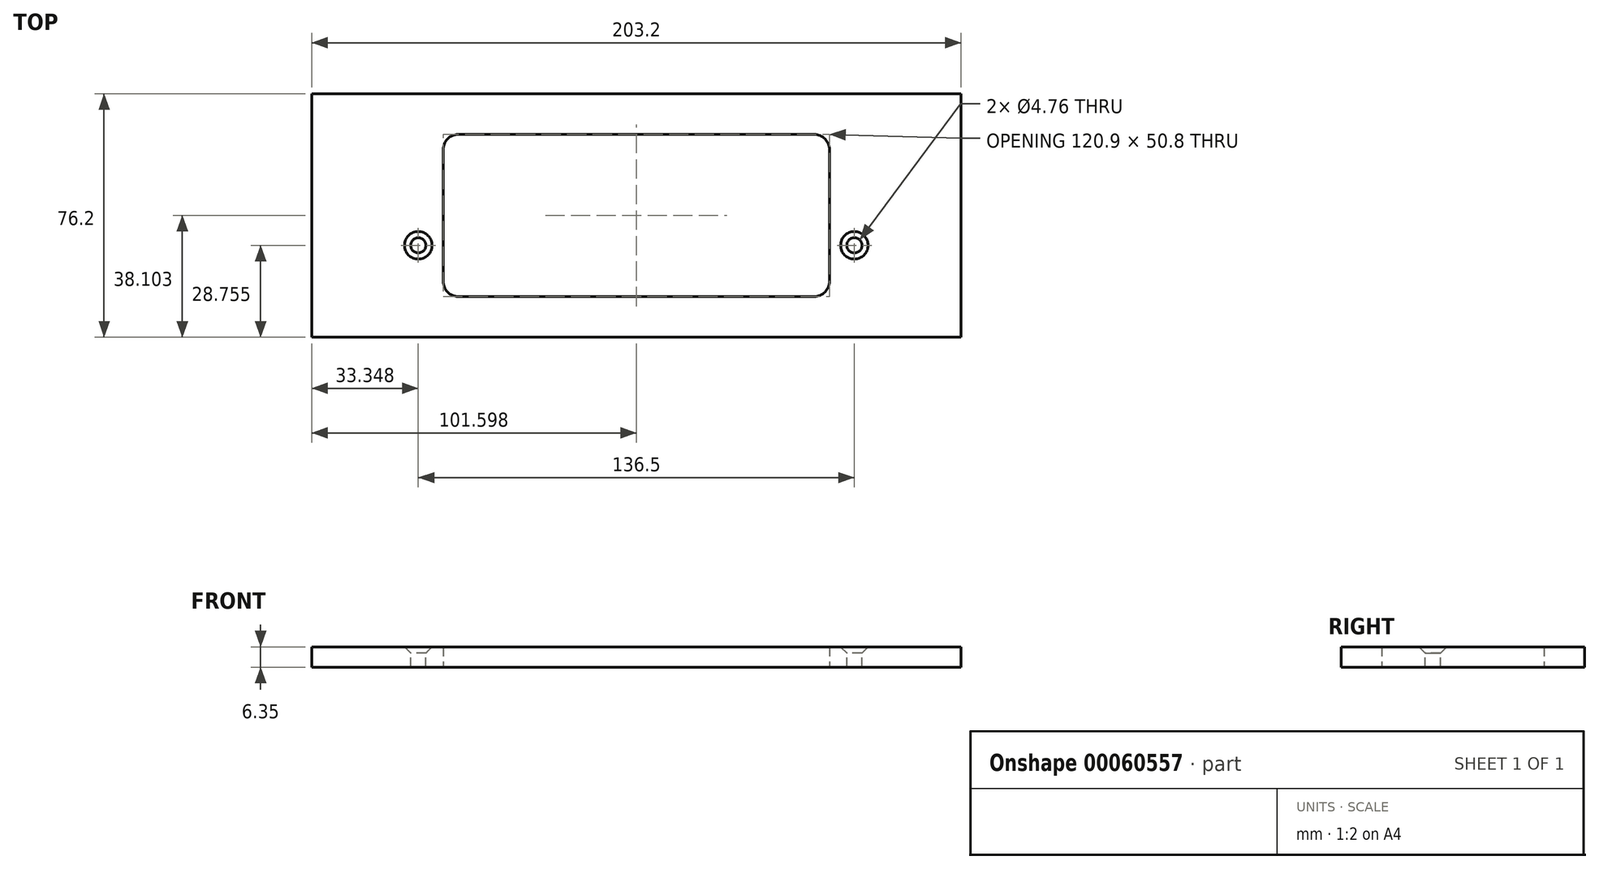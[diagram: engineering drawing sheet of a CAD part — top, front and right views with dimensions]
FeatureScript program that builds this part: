
annotation { "Feature Type Name" : "Feature", "Feature Type Description" : "" }
export const myFeature = defineFeature(function(context is Context, id is Id, definition is map)
    precondition{}
    {
        {
            var Q0;
            Q0=qCreatedBy(makeId("Top.planeOp"),FACE);
            var sketch = newSketch(context, id + "F0", { "sketchPlane" : qUnion([Q0])});
            skLineSegment(sketch, "E0.top", {"start": v(-103.7, -42.69) * mm, "end": v(99.5, -42.69) * mm});
            skLineSegment(sketch, "E0.left", {"start": v(-103.7, 33.51) * mm, "end": v(-103.7, -42.69) * mm});
            skLineSegment(sketch, "E0.right", {"start": v(99.5, 33.51) * mm, "end": v(99.5, -42.69) * mm});
            skPoint(sketch, "E1.rect.middle", {"position": v(0, 0) * mm});
            skLineSegment(sketch, "E2", {"start": v(-103.7, 33.51) * mm, "end": v(99.5, 33.51) * mm});
            skLineSegment(sketch, "E3.bottom", {"start": v(-57.78, 20.81) * mm, "end": v(53.6, 20.81) * mm});
            skLineSegment(sketch, "E3.top", {"start": v(-57.78, -29.99) * mm, "end": v(53.6, -29.99) * mm});
            skLineSegment(sketch, "E3.left", {"start": v(-62.54, 16.05) * mm, "end": v(-62.54, -25.22) * mm});
            skLineSegment(sketch, "E3.right", {"start": v(58.36, 16.05) * mm, "end": v(58.36, -25.22) * mm});
            skPoint(sketch, "E4.visualSharp", {"position": v(-62.54, 20.81) * mm});
            skArc(sketch, "E4.filletArc", {"start": v(-57.78, 20.81) * mm, "mid": v(-61.15, 19.42) * mm, "end": v(-62.54, 16.05) * mm});
            skPoint(sketch, "E5.visualSharp", {"position": v(-62.54, -29.99) * mm});
            skArc(sketch, "E5.filletArc", {"start": v(-62.54, -25.22) * mm, "mid": v(-61.15, -28.6) * mm, "end": v(-57.78, -29.99) * mm});
            skPoint(sketch, "E6.visualSharp", {"position": v(58.36, 20.81) * mm});
            skArc(sketch, "E6.filletArc", {"start": v(58.36, 16.05) * mm, "mid": v(56.97, 19.42) * mm, "end": v(53.6, 20.81) * mm});
            skPoint(sketch, "E7.visualSharp", {"position": v(58.36, -29.99) * mm});
            skArc(sketch, "E7.filletArc", {"start": v(53.6, -29.99) * mm, "mid": v(56.97, -28.6) * mm, "end": v(58.36, -25.22) * mm});
            skSolve(sketch);
        }
        {
            var Q0;
            Q0=makeQuery(id+"F0.imprint","IMPRINT",FACE,{"disambiguationData":[TD([[makeQuery(id+"F0.imprint","IMPRINT",EDGE,{"derivedFrom":sQuery(id+"F0.wireOp",EDGE,"E0.top")}),1.0]])]});
            extrude(context, id + "F1", {"entities" : qUnion([Q0]), "depth" : 6.35 * mm});
        }
        {
            var Q0;
            Q0=makeQuery(id+"F1.opExtrude","CAP_FACE",FACE,{"disambiguationData":[OSD([sQuery(id+"F0.wireOp",EDGE,"E0.top"),sQuery(id+"F0.wireOp",EDGE,"E0.left"),sQuery(id+"F0.wireOp",EDGE,"E0.right"),sQuery(id+"F0.wireOp",EDGE,"E2"),sQuery(id+"F0.wireOp",EDGE,"E3.bottom"),sQuery(id+"F0.wireOp",EDGE,"E3.top"),sQuery(id+"F0.wireOp",EDGE,"E3.left"),sQuery(id+"F0.wireOp",EDGE,"E3.right"),sQuery(id+"F0.wireOp",EDGE,"E4.filletArc"),sQuery(id+"F0.wireOp",EDGE,"E5.filletArc"),sQuery(id+"F0.wireOp",EDGE,"E6.filletArc"),sQuery(id+"F0.wireOp",EDGE,"E7.filletArc")])],"isStart":false});
            var sketch = newSketch(context, id + "F2", { "sketchPlane" : qUnion([Q0])});
            skSolve(sketch);
        }
        {
            var Q0;
            Q0=makeQuery(id+"F2.imprint","IMPRINT",FACE,{"disambiguationData":[TD([[makeQuery(id+"F2.imprint","IMPRINT",EDGE,{"derivedFrom":makeQuery(id+"F1.opExtrude","CAP_EDGE",EDGE,{"disambiguationData":[OSD([sQuery(id+"F0.wireOp",EDGE,"E0.top")])],"isStart":false})}),1.0]])]});
            var sketch = newSketch(context, id + "F3", { "sketchPlane" : qUnion([Q0])});
            skPoint(sketch, "E8", {"position": v(-2.1, -30.17) * mm});
            skPoint(sketch, "E9", {"position": v(-70.34, -13.93) * mm});
            skPoint(sketch, "E10", {"position": v(66.16, -13.93) * mm});
            skSolve(sketch);
        }
        {
            var Q0;
            Q0=sQuery(id+"F3.wireOp",VERTEX,"E9");
            var Q1;
            Q1=sQuery(id+"F3.wireOp",VERTEX,"E10");
            var Q2;
            Q2=makeQuery(id+"F1.opExtrude","SWEPT_BODY",BODY,{"disambiguationData":[OSD([sQuery(id+"F0.wireOp",EDGE,"E0.top"),sQuery(id+"F0.wireOp",EDGE,"E0.left"),sQuery(id+"F0.wireOp",EDGE,"E0.right"),sQuery(id+"F0.wireOp",EDGE,"E2"),sQuery(id+"F0.wireOp",EDGE,"E3.bottom"),sQuery(id+"F0.wireOp",EDGE,"E3.top"),sQuery(id+"F0.wireOp",EDGE,"E3.left"),sQuery(id+"F0.wireOp",EDGE,"E3.right"),sQuery(id+"F0.wireOp",EDGE,"E4.filletArc"),sQuery(id+"F0.wireOp",EDGE,"E5.filletArc"),sQuery(id+"F0.wireOp",EDGE,"E6.filletArc"),sQuery(id+"F0.wireOp",EDGE,"E7.filletArc")])]});
            hole(context, id + "F4", {"style" : HoleStyle.C_SINK, "holeDiameter" : 4.76 * mm, "cSinkDiameter" : 8.6 * mm, "endStyle" : HoleEndStyle.THROUGH, "locations" : qUnion([Q0, Q1]), "scope" : qUnion([Q2]), "cSinkAngle" : 90 * degree});
        }
    });
